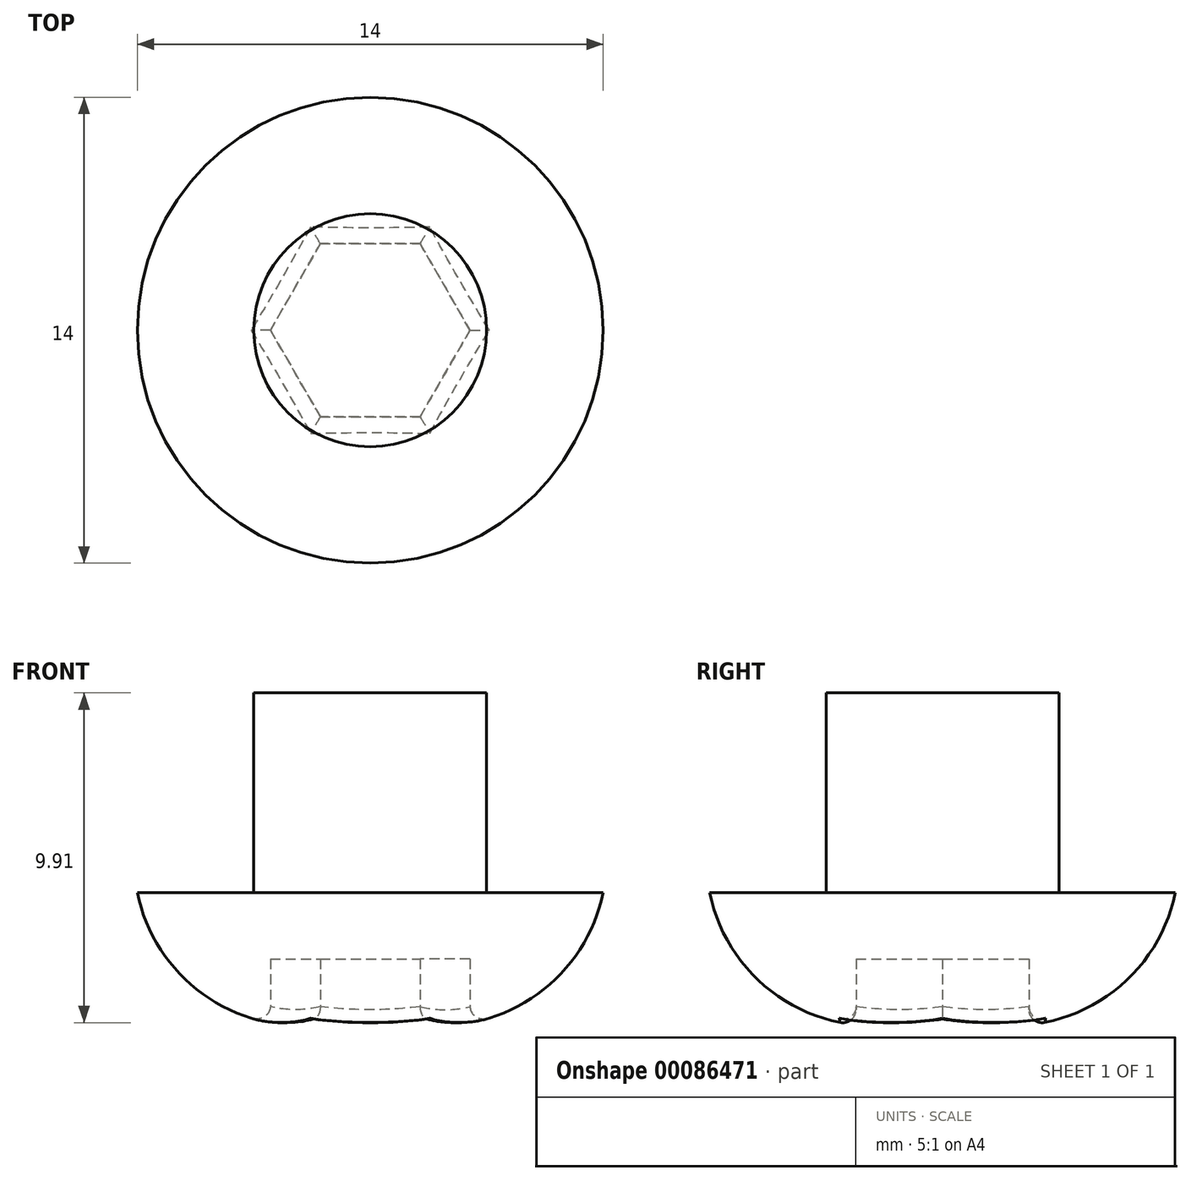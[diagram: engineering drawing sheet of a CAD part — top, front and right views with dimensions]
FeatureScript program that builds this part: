
annotation { "Feature Type Name" : "Feature", "Feature Type Description" : "" }
export const myFeature = defineFeature(function(context is Context, id is Id, definition is map)
    precondition{}
    {
        {
            var Q0;
            Q0=qCreatedBy(makeId("Top.planeOp"),FACE);
            var sketch = newSketch(context, id + "F0", { "sketchPlane" : qUnion([Q0])});
            skCircle(sketch, "E0", {"center": v(0, 0) * mm, "radius": 3.5 * mm});
            skSolve(sketch);
        }
        {
            var Q0;
            Q0=qSketchRegion(id+"F0",true);
            extrude(context, id + "F1", {"entities" : qUnion([Q0]), "depth" : 10 * mm});
        }
        {
            var Q0;
            Q0=qCreatedBy(makeId("Top.planeOp"),FACE);
            var sketch = newSketch(context, id + "F2", { "sketchPlane" : qUnion([Q0])});
            skCircle(sketch, "E1", {"center": v(0, 0) * mm, "radius": 7 * mm});
            skSolve(sketch);
        }
        {
            var Q0;
            Q0=qSketchRegion(id+"F2",true);
            extrude(context, id + "F3", {"entities" : qUnion([Q0]), "operationType" : NewBodyOperationType.ADD, "depth" : 4 * mm});
        }
        {
            var Q0;
            Q0=makeQuery(id+"F3.opExtrude","CAP_EDGE",EDGE,{"disambiguationData":[OSD([sQuery(id+"F2.wireOp",EDGE,"E1")])],"isStart":true});
            fillet(context, id + "F4", {"entities" : qUnion([Q0]), "radius" : 5 * mm, "tangentPropagation" : true, "allowEdgeOverflow" : false});
        }
        {
            var Q0;
            Q0=makeQuery(id+"F3.boolean.opBoolean","MERGE",FACE,{"derivedFrom":[makeQuery(id+"F1.opExtrude","CAP_FACE",FACE,{"disambiguationData":[OSD([sQuery(id+"F0.wireOp",EDGE,"E0")])],"isStart":true}),makeQuery(id+"F3.opExtrude","CAP_FACE",FACE,{"disambiguationData":[OSD([sQuery(id+"F2.wireOp",EDGE,"E1")])],"isStart":true})]});
            var sketch = newSketch(context, id + "F5", { "sketchPlane" : qUnion([Q0])});
            skCircle(sketch, "E2.cCircle", {"center": v(0, 0) * mm, "radius": 3 * mm, "construction": true});
            skLineSegment(sketch, "E2.0", {"start": v(3, 0) * mm, "end": v(1.5, -2.6) * mm});
            skLineSegment(sketch, "E2.1", {"start": v(1.5, -2.6) * mm, "end": v(-1.5, -2.6) * mm});
            skLineSegment(sketch, "E2.2", {"start": v(-1.5, -2.6) * mm, "end": v(-3, 0) * mm});
            skLineSegment(sketch, "E2.3", {"start": v(-3, 0) * mm, "end": v(-1.5, 2.6) * mm});
            skLineSegment(sketch, "E2.4", {"start": v(-1.5, 2.6) * mm, "end": v(1.5, 2.6) * mm});
            skLineSegment(sketch, "E2.5", {"start": v(1.5, 2.6) * mm, "end": v(3, 0) * mm});
            skSolve(sketch);
        }
        {
            var Q0;
            Q0=qSketchRegion(id+"F5",true);
            extrude(context, id + "F6", {"entities" : qUnion([Q0]), "operationType" : NewBodyOperationType.REMOVE, "oppositeDirection" : true, "depth" : 2 * mm});
        }
        {
            var Q0;
            Q0=makeQuery(id+"F6.boolean.opBoolean","INTERSECT",EDGE,{"derivedFrom":[makeQuery(id+"F4.opFillet","BLEND_FACE",FACE,{"disambiguationData":[OSD([sQuery(id+"F2.wireOp",EDGE,"E1")])]}),makeQuery(id+"F6.opExtrude","SWEPT_FACE",FACE,{"disambiguationData":[OSD([sQuery(id+"F5.wireOp",EDGE,"E2.3")])]})]});
            var Q1;
            Q1=makeQuery(id+"F6.boolean.opBoolean","INTERSECT",EDGE,{"derivedFrom":[makeQuery(id+"F4.opFillet","BLEND_FACE",FACE,{"disambiguationData":[OSD([sQuery(id+"F2.wireOp",EDGE,"E1")])]}),makeQuery(id+"F6.opExtrude","SWEPT_FACE",FACE,{"disambiguationData":[OSD([sQuery(id+"F5.wireOp",EDGE,"E2.2")])]})]});
            var Q2;
            Q2=makeQuery(id+"F6.boolean.opBoolean","INTERSECT",EDGE,{"derivedFrom":[makeQuery(id+"F4.opFillet","BLEND_FACE",FACE,{"disambiguationData":[OSD([sQuery(id+"F2.wireOp",EDGE,"E1")])]}),makeQuery(id+"F6.opExtrude","SWEPT_FACE",FACE,{"disambiguationData":[OSD([sQuery(id+"F5.wireOp",EDGE,"E2.1")])]})]});
            var Q3;
            Q3=makeQuery(id+"F6.boolean.opBoolean","INTERSECT",EDGE,{"derivedFrom":[makeQuery(id+"F4.opFillet","BLEND_FACE",FACE,{"disambiguationData":[OSD([sQuery(id+"F2.wireOp",EDGE,"E1")])]}),makeQuery(id+"F6.opExtrude","SWEPT_FACE",FACE,{"disambiguationData":[OSD([sQuery(id+"F5.wireOp",EDGE,"E2.0")])]})]});
            var Q4;
            Q4=makeQuery(id+"F6.boolean.opBoolean","INTERSECT",EDGE,{"derivedFrom":[makeQuery(id+"F4.opFillet","BLEND_FACE",FACE,{"disambiguationData":[OSD([sQuery(id+"F2.wireOp",EDGE,"E1")])]}),makeQuery(id+"F6.opExtrude","SWEPT_FACE",FACE,{"disambiguationData":[OSD([sQuery(id+"F5.wireOp",EDGE,"E2.5")])]})]});
            var Q5;
            Q5=makeQuery(id+"F6.boolean.opBoolean","INTERSECT",EDGE,{"derivedFrom":[makeQuery(id+"F4.opFillet","BLEND_FACE",FACE,{"disambiguationData":[OSD([sQuery(id+"F2.wireOp",EDGE,"E1")])]}),makeQuery(id+"F6.opExtrude","SWEPT_FACE",FACE,{"disambiguationData":[OSD([sQuery(id+"F5.wireOp",EDGE,"E2.4")])]})]});
            fillet(context, id + "F7", {"entities" : qUnion([Q0, Q1, Q2, Q3, Q4, Q5]), "radius" : .4 * mm, "tangentPropagation" : true, "allowEdgeOverflow" : false});
        }
    });
